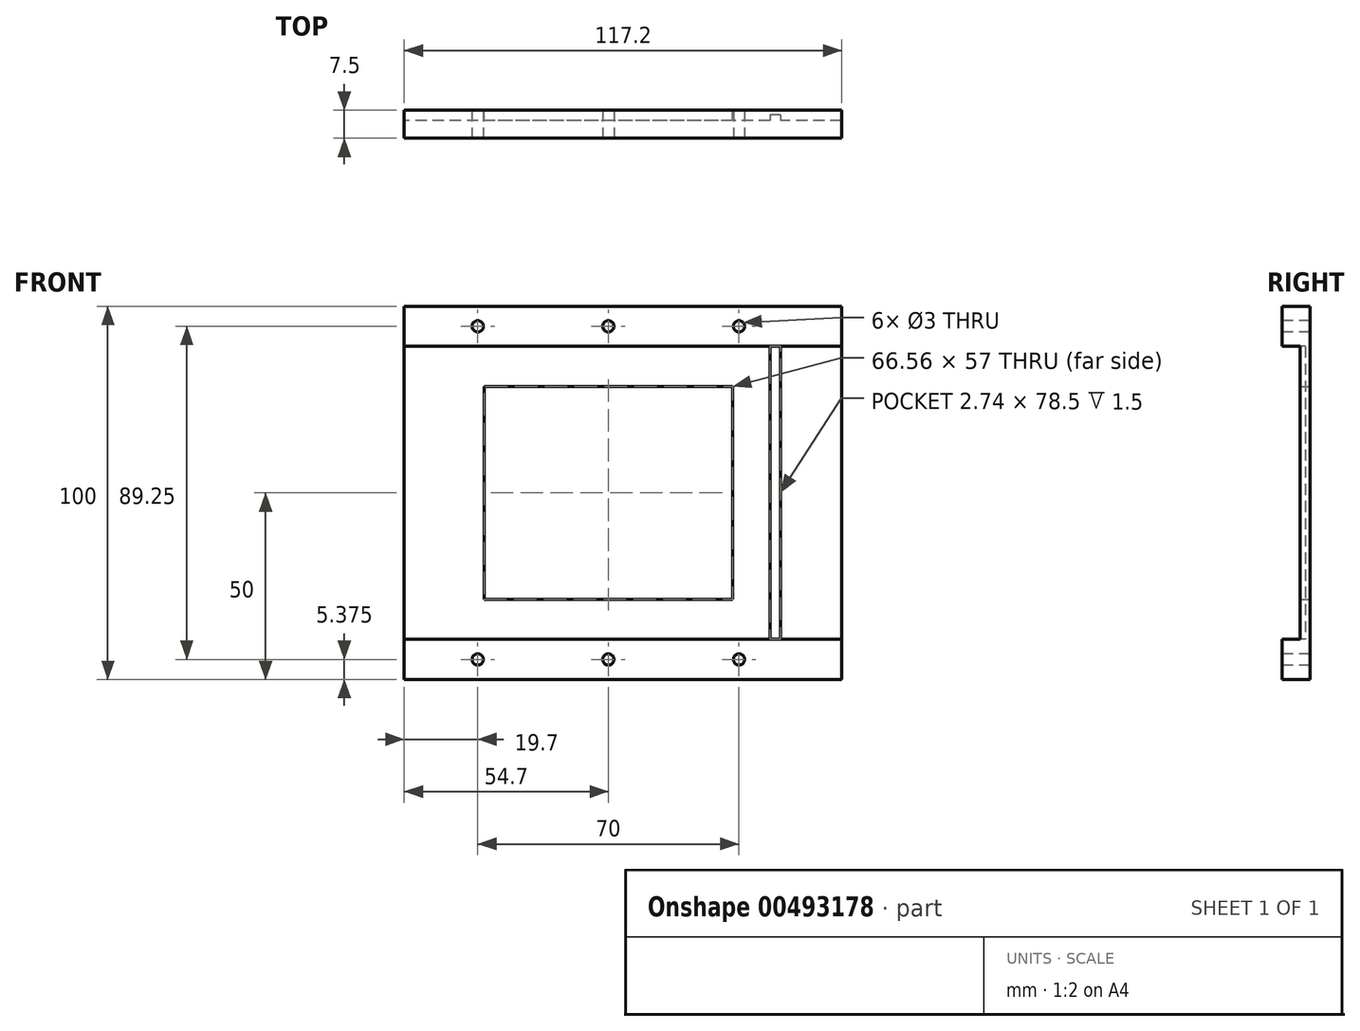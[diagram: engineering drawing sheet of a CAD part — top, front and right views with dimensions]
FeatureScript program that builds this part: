
annotation { "Feature Type Name" : "Feature", "Feature Type Description" : "" }
export const myFeature = defineFeature(function(context is Context, id is Id, definition is map)
    precondition{}
    {
        {
            var Q0;
            Q0=qCreatedBy(makeId("Front.planeOp"),FACE);
            var sketch = newSketch(context, id + "F0", { "sketchPlane" : qUnion([Q0])});
            skLineSegment(sketch, "E0.bottom", {"start": v(51.9, 39.25) * mm, "end": v(-51.9, 39.25) * mm, "construction": true});
            skLineSegment(sketch, "E0.top", {"start": v(51.9, -39.25) * mm, "end": v(-51.9, -39.25) * mm, "construction": true});
            skLineSegment(sketch, "E0.left", {"start": v(51.9, 39.25) * mm, "end": v(51.9, -39.25) * mm, "construction": true});
            skLineSegment(sketch, "E0.right", {"start": v(-51.9, 39.25) * mm, "end": v(-51.9, -39.25) * mm, "construction": true});
            skPoint(sketch, "E0.middle", {"position": v(0, 0) * mm});
            skLineSegment(sketch, "E1.bottom", {"start": v(33.28, 28.5) * mm, "end": v(-33.28, 28.5) * mm});
            skLineSegment(sketch, "E1.top", {"start": v(33.28, -28.5) * mm, "end": v(-33.28, -28.5) * mm});
            skLineSegment(sketch, "E1.left", {"start": v(33.28, 28.5) * mm, "end": v(33.28, -28.5) * mm});
            skLineSegment(sketch, "E1.right", {"start": v(-33.28, 28.5) * mm, "end": v(-33.28, -28.5) * mm});
            skLineSegment(sketch, "E2.bottom", {"start": v(62.5, 50) * mm, "end": v(-62.5, 50) * mm});
            skLineSegment(sketch, "E2.top", {"start": v(62.5, -50) * mm, "end": v(-62.5, -50) * mm});
            skLineSegment(sketch, "E2.left", {"start": v(62.5, 50) * mm, "end": v(62.5, -50) * mm});
            skLineSegment(sketch, "E2.right", {"start": v(-62.5, 50) * mm, "end": v(-62.5, -50) * mm});
            skSolve(sketch);
        }
        {
            var Q0;
            Q0=qSketchRegion(id+"F0",true);
            extrude(context, id + "F1", {"entities" : qUnion([Q0]), "depth" : 7.5 * mm});
        }
        {
            var Q0;
            Q0=makeQuery(id+"F1.opExtrude","CAP_FACE",FACE,{"disambiguationData":[OSD([sQuery(id+"F0.wireOp",EDGE,"E1.bottom"),sQuery(id+"F0.wireOp",EDGE,"E1.top"),sQuery(id+"F0.wireOp",EDGE,"E1.left"),sQuery(id+"F0.wireOp",EDGE,"E1.right"),sQuery(id+"F0.wireOp",EDGE,"E2.bottom"),sQuery(id+"F0.wireOp",EDGE,"E2.top"),sQuery(id+"F0.wireOp",EDGE,"E2.left"),sQuery(id+"F0.wireOp",EDGE,"E2.right")])],"isStart":false});
            var sketch = newSketch(context, id + "F2", { "sketchPlane" : qUnion([Q0])});
            skLineSegment(sketch, "E3.bottom", {"start": v(87.32, 39.25) * mm, "end": v(-87.32, 39.25) * mm});
            skLineSegment(sketch, "E3.top", {"start": v(87.32, -39.25) * mm, "end": v(-87.32, -39.25) * mm});
            skLineSegment(sketch, "E3.left", {"start": v(87.32, 39.25) * mm, "end": v(87.32, -39.25) * mm});
            skLineSegment(sketch, "E3.right", {"start": v(-87.32, 39.25) * mm, "end": v(-87.32, -39.25) * mm});
            skPoint(sketch, "E3.middle", {"position": v(0, 0) * mm});
            skSolve(sketch);
        }
        {
            var Q0;
            Q0 = qSketchRegion(id + "F2", true);
            extrude(context, id + "F3", {"entities" : qUnion([Q0]), "operationType" : NewBodyOperationType.REMOVE, "oppositeDirection" : true, "depth" : 4.75 * mm});
        }
        {
            var Q0;
            Q0=makeQuery(id+"F3.boolean.opBoolean","COPY",FACE,{"derivedFrom":makeQuery(id+"F3.opExtrude","CAP_FACE",FACE,{"disambiguationData":[OSD([sQuery(id+"F2.wireOp",EDGE,"E3.bottom"),sQuery(id+"F2.wireOp",EDGE,"E3.top"),sQuery(id+"F2.wireOp",EDGE,"E3.left"),sQuery(id+"F2.wireOp",EDGE,"E3.right")])],"isStart":false})});
            var sketch = newSketch(context, id + "F4", { "sketchPlane" : qUnion([Q0])});
            skLineSegment(sketch, "E4.bottom", {"start": v(43.32, 39.25) * mm, "end": v(46.06, 39.25) * mm});
            skLineSegment(sketch, "E4.top", {"start": v(43.32, -39.25) * mm, "end": v(46.06, -39.25) * mm});
            skLineSegment(sketch, "E4.left", {"start": v(46.06, 39.25) * mm, "end": v(46.06, -39.25) * mm});
            skLineSegment(sketch, "E4.right", {"start": v(43.32, 39.25) * mm, "end": v(43.32, -39.25) * mm});
            skSolve(sketch);
        }
        {
            var Q0;
            Q0 = qSketchRegion(id + "F4", true);
            extrude(context, id + "F5", {"entities" : qUnion([Q0]), "operationType" : NewBodyOperationType.REMOVE, "oppositeDirection" : true, "depth" : 1.5 * mm});
        }
        {
            var Q0;
            {var subQ0=sQuery(id+"F2.wireOp",EDGE,"E3.bottom");var subQ1=sQuery(id+"F2.wireOp",EDGE,"E3.top");Q0=makeQuery(id+"F5.boolean.opBoolean","SPLIT",FACE,{"disambiguationData":[TD([makeQuery(id+"F1.opExtrude","SWEPT_FACE",FACE,{"disambiguationData":[OSD([sQuery(id+"F0.wireOp",EDGE,"E1.bottom")])]})])],"derivedFrom":makeQuery(id+"F3.boolean.opBoolean","COPY",FACE,{"derivedFrom":makeQuery(id+"F3.opExtrude","CAP_FACE",FACE,{"disambiguationData":[OSD([subQ0,subQ1,sQuery(id+"F2.wireOp",EDGE,"E3.left"),sQuery(id+"F2.wireOp",EDGE,"E3.right")])],"isStart":false})})});}
            var sketch = newSketch(context, id + "F6", { "sketchPlane" : qUnion([Q0])});
            skLineSegment(sketch, "E5.bottom", {"start": v(-62.5, 39.25) * mm, "end": v(-54.7, 39.25) * mm});
            skLineSegment(sketch, "E5.top", {"start": v(-62.5, -39.25) * mm, "end": v(-54.7, -39.25) * mm});
            skLineSegment(sketch, "E5.left", {"start": v(-62.5, 39.25) * mm, "end": v(-62.5, -39.25) * mm});
            skLineSegment(sketch, "E5.right", {"start": v(-54.7, 39.25) * mm, "end": v(-54.7, -39.25) * mm});
            skSolve(sketch);
        }
        {
            var Q0;
            Q0 = qSketchRegion(id + "F6", true);
            extrude(context, id + "F7", {"entities" : qUnion([Q0]), "operationType" : NewBodyOperationType.ADD, "depth" : 4.75 * mm});
        }
        {
            var Q0;
            {var subQ0=sQuery(id+"F0.wireOp",EDGE,"E2.top");var subQ1=sQuery(id+"F0.wireOp",EDGE,"E2.left");var subQ3=sQuery(id+"F0.wireOp",EDGE,"E2.right");var subQ5=sQuery(id+"F0.wireOp",EDGE,"E2.bottom");var subQ6=makeQuery(id+"F1.opExtrude","CAP_FACE",FACE,{"disambiguationData":[OSD([sQuery(id+"F0.wireOp",EDGE,"E1.bottom"),sQuery(id+"F0.wireOp",EDGE,"E1.top"),sQuery(id+"F0.wireOp",EDGE,"E1.left"),sQuery(id+"F0.wireOp",EDGE,"E1.right"),subQ5,subQ0,subQ1,subQ3])],"isStart":false});Q0=makeQuery(id+"F7.boolean.opBoolean","MERGE",FACE,{"derivedFrom":[makeQuery(id+"F3.boolean.opBoolean","SPLIT",FACE,{"disambiguationData":[TD([makeQuery(id+"F1.opExtrude","SWEPT_FACE",FACE,{"disambiguationData":[OSD([subQ5])]})])],"derivedFrom":subQ6}),makeQuery(id+"F3.boolean.opBoolean","SPLIT",FACE,{"disambiguationData":[TD([makeQuery(id+"F1.opExtrude","SWEPT_FACE",FACE,{"disambiguationData":[OSD([subQ0])]})])],"derivedFrom":subQ6}),makeQuery(id+"F7.opExtrude","CAP_FACE",FACE,{"disambiguationData":[OSD([sQuery(id+"F6.wireOp",EDGE,"E5.bottom"),sQuery(id+"F6.wireOp",EDGE,"E5.top"),sQuery(id+"F6.wireOp",EDGE,"E5.left"),sQuery(id+"F6.wireOp",EDGE,"E5.right")])],"isStart":false})]});}
            var sketch = newSketch(context, id + "F8", { "sketchPlane" : qUnion([Q0])});
            skLineSegment(sketch, "E6.bottom", {"start": v(-62.5, 50) * mm, "end": v(-54.7, 50) * mm});
            skLineSegment(sketch, "E6.top", {"start": v(-62.5, -50) * mm, "end": v(-54.7, -50) * mm});
            skLineSegment(sketch, "E6.left", {"start": v(-62.5, 50) * mm, "end": v(-62.5, -50) * mm});
            skLineSegment(sketch, "E6.right", {"start": v(-54.7, 50) * mm, "end": v(-54.7, -50) * mm});
            skSolve(sketch);
        }
        {
            var Q0;
            Q0 = qSketchRegion(id + "F8", true);
            extrude(context, id + "F9", {"entities" : qUnion([Q0]), "operationType" : NewBodyOperationType.REMOVE, "oppositeDirection" : true, "depth" : 25 * mm});
        }
        {
            var Q0;
            {var subQ0=sQuery(id+"F0.wireOp",EDGE,"E2.bottom");var subQ1=makeQuery(id+"F1.opExtrude","SWEPT_FACE",FACE,{"disambiguationData":[OSD([subQ0])]});var subQ3=sQuery(id+"F0.wireOp",EDGE,"E2.left");var subQ5=sQuery(id+"F0.wireOp",EDGE,"E2.top");var subQ6=sQuery(id+"F0.wireOp",EDGE,"E2.right");var subQ8=makeQuery(id+"F1.opExtrude","CAP_FACE",FACE,{"disambiguationData":[OSD([sQuery(id+"F0.wireOp",EDGE,"E1.bottom"),sQuery(id+"F0.wireOp",EDGE,"E1.top"),sQuery(id+"F0.wireOp",EDGE,"E1.left"),sQuery(id+"F0.wireOp",EDGE,"E1.right"),subQ0,subQ5,subQ3,subQ6])],"isStart":false});Q0=makeQuery(id+"F9.boolean.opBoolean","SPLIT",FACE,{"disambiguationData":[TD([subQ1])],"derivedFrom":makeQuery(id+"F7.boolean.opBoolean","MERGE",FACE,{"derivedFrom":[makeQuery(id+"F3.boolean.opBoolean","SPLIT",FACE,{"disambiguationData":[TD([subQ1])],"derivedFrom":subQ8}),makeQuery(id+"F3.boolean.opBoolean","SPLIT",FACE,{"disambiguationData":[TD([makeQuery(id+"F1.opExtrude","SWEPT_FACE",FACE,{"disambiguationData":[OSD([subQ5])]})])],"derivedFrom":subQ8}),makeQuery(id+"F7.opExtrude","CAP_FACE",FACE,{"disambiguationData":[OSD([sQuery(id+"F6.wireOp",EDGE,"E5.bottom"),sQuery(id+"F6.wireOp",EDGE,"E5.top"),sQuery(id+"F6.wireOp",EDGE,"E5.left"),sQuery(id+"F6.wireOp",EDGE,"E5.right")])],"isStart":false})]})});}
            var sketch = newSketch(context, id + "F10", { "sketchPlane" : qUnion([Q0])});
            skLineSegment(sketch, "E7", {"start": v(0, 50) * mm, "end": v(0, -50.1) * mm, "construction": true});
            skLineSegment(sketch, "E8", {"start": v(-54.7, 39.25) * mm, "end": v(-54.7, 50) * mm, "construction": true});
            skLineSegment(sketch, "E9", {"start": v(-54.7, 44.63) * mm, "end": v(62.5, 44.63) * mm, "construction": true});
            skCircle(sketch, "E10", {"center": v(0, 44.63) * mm, "radius": 1.5 * mm});
            skCircle(sketch, "E11", {"center": v(-35, 44.62) * mm, "radius": 1.5 * mm});
            skCircle(sketch, "E12", {"center": v(35, 44.62) * mm, "radius": 1.5 * mm});
            skSolve(sketch);
        }
        {
            var Q0;
            Q0 = qSketchRegion(id + "F10", true);
            extrude(context, id + "F11", {"entities" : qUnion([Q0]), "operationType" : NewBodyOperationType.REMOVE, "oppositeDirection" : true, "depth" : 25 * mm});
        }
        {
            var Q0;
            {var subQ1=sQuery(id+"F0.wireOp",EDGE,"E2.top");var subQ2=makeQuery(id+"F1.opExtrude","SWEPT_FACE",FACE,{"disambiguationData":[OSD([subQ1])]});var subQ3=sQuery(id+"F0.wireOp",EDGE,"E2.left");var subQ5=sQuery(id+"F0.wireOp",EDGE,"E2.right");var subQ7=sQuery(id+"F0.wireOp",EDGE,"E2.bottom");var subQ8=makeQuery(id+"F1.opExtrude","CAP_FACE",FACE,{"disambiguationData":[OSD([sQuery(id+"F0.wireOp",EDGE,"E1.bottom"),sQuery(id+"F0.wireOp",EDGE,"E1.top"),sQuery(id+"F0.wireOp",EDGE,"E1.left"),sQuery(id+"F0.wireOp",EDGE,"E1.right"),subQ7,subQ1,subQ3,subQ5])],"isStart":false});Q0=makeQuery(id+"F9.boolean.opBoolean","SPLIT",FACE,{"disambiguationData":[TD([subQ2])],"derivedFrom":makeQuery(id+"F7.boolean.opBoolean","MERGE",FACE,{"derivedFrom":[makeQuery(id+"F3.boolean.opBoolean","SPLIT",FACE,{"disambiguationData":[TD([makeQuery(id+"F1.opExtrude","SWEPT_FACE",FACE,{"disambiguationData":[OSD([subQ7])]})])],"derivedFrom":subQ8}),makeQuery(id+"F3.boolean.opBoolean","SPLIT",FACE,{"disambiguationData":[TD([subQ2])],"derivedFrom":subQ8}),makeQuery(id+"F7.opExtrude","CAP_FACE",FACE,{"disambiguationData":[OSD([sQuery(id+"F6.wireOp",EDGE,"E5.bottom"),sQuery(id+"F6.wireOp",EDGE,"E5.top"),sQuery(id+"F6.wireOp",EDGE,"E5.left"),sQuery(id+"F6.wireOp",EDGE,"E5.right")])],"isStart":false})]})});}
            var sketch = newSketch(context, id + "F12", { "sketchPlane" : qUnion([Q0])});
            skLineSegment(sketch, "E13", {"start": v(-54.7, -39.25) * mm, "end": v(-54.7, -50) * mm, "construction": true});
            skLineSegment(sketch, "E14", {"start": v(-54.7, -50) * mm, "end": v(-54.7, -44.63) * mm, "construction": true});
            skLineSegment(sketch, "E15", {"start": v(-54.7, -44.63) * mm, "end": v(62.5, -44.63) * mm, "construction": true});
            skCircle(sketch, "E16", {"center": v(0, -44.63) * mm, "radius": 1.5 * mm});
            skCircle(sketch, "E17", {"center": v(35, -44.62) * mm, "radius": 1.5 * mm});
            skCircle(sketch, "E18", {"center": v(-35, -44.62) * mm, "radius": 1.5 * mm});
            skSolve(sketch);
        }
        {
            var Q0;
            Q0 = qSketchRegion(id + "F12", true);
            extrude(context, id + "F13", {"entities" : qUnion([Q0]), "operationType" : NewBodyOperationType.REMOVE, "oppositeDirection" : true, "depth" : 25 * mm});
        }
    });
